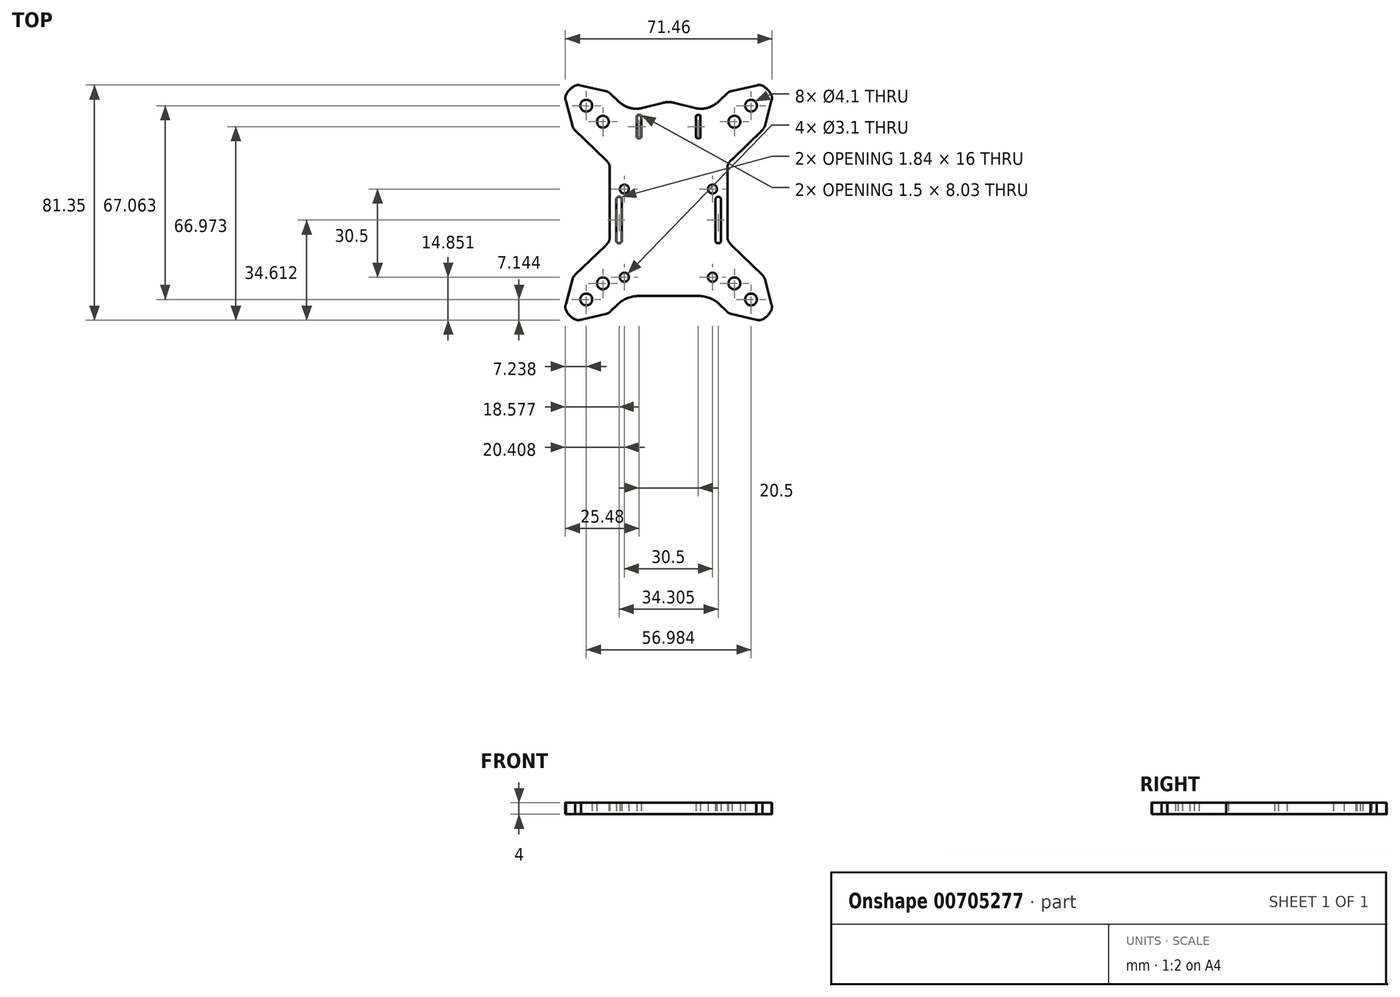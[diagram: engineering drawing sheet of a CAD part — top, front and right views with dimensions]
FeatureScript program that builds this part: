
annotation { "Feature Type Name" : "Feature", "Feature Type Description" : "" }
export const myFeature = defineFeature(function(context is Context, id is Id, definition is map)
    precondition{}
    {
        {
            var Q0;
            Q0=qCreatedBy(makeId("Top.planeOp"),FACE);
            var sketch = newSketch(context, id + "F0", { "sketchPlane" : qUnion([Q0])});
            skArc(sketch, "E0.MirrorCS", {"start": v(21.65, -41.5) * mm, "mid": v(20.88, -41.2) * mm, "end": v(20.23, -40.73) * mm});
            skArc(sketch, "E1.MirrorCS", {"start": v(32.4, -43.4) * mm, "mid": v(31.36, -43.62) * mm, "end": v(30.33, -43.46) * mm});
            skLineSegment(sketch, "E2.MirrorCS", {"start": v(19.47, -40) * mm, "end": v(20.23, -40.73) * mm});
            skArc(sketch, "E3.MirrorCS", {"start": v(35.55, -40.13) * mm, "mid": v(34.25, -42.03) * mm, "end": v(32.4, -43.4) * mm});
            skLineSegment(sketch, "E4.MirrorCS", {"start": v(30.33, -43.46) * mm, "end": v(25.04, -42.26) * mm});
            skLineSegment(sketch, "E5.MirrorCS", {"start": v(25.04, -42.26) * mm, "end": v(21.65, -41.5) * mm});
            skLineSegment(sketch, "E6.MirrorCS", {"start": v(34.15, -32.83) * mm, "end": v(33.26, -29.46) * mm});
            skArc(sketch, "E7.MirrorCS", {"start": v(32.45, -28.06) * mm, "mid": v(32.95, -28.7) * mm, "end": v(33.26, -29.46) * mm});
            skArc(sketch, "E8.MirrorCS", {"start": v(35.55, -40.13) * mm, "mid": v(35.73, -39.1) * mm, "end": v(35.54, -38.06) * mm});
            skLineSegment(sketch, "E9.MirrorCS", {"start": v(35.54, -38.06) * mm, "end": v(34.15, -32.83) * mm});
            skCircle(sketch, "E10.MirrorC", {"center": v(28.5, -36.48) * mm, "radius": 2.05 * mm});
            skLineSegment(sketch, "E11.MirrorCS", {"start": v(19.47, -40) * mm, "end": v(17.5, -38.1) * mm});
            skLineSegment(sketch, "E12.MirrorCS", {"start": v(-19.47, -40) * mm, "end": v(-20.23, -40.73) * mm});
            skArc(sketch, "E13.MirrorCS", {"start": v(-21.65, -41.5) * mm, "mid": v(-20.88, -41.2) * mm, "end": v(-20.23, -40.73) * mm});
            skArc(sketch, "E14.MirrorCS", {"start": v(-32.45, -28.06) * mm, "mid": v(-32.95, -28.7) * mm, "end": v(-33.26, -29.46) * mm});
            skArc(sketch, "E15.MirrorCS", {"start": v(-32.4, -43.4) * mm, "mid": v(-31.36, -43.62) * mm, "end": v(-30.33, -43.46) * mm});
            skLineSegment(sketch, "E16.MirrorCS", {"start": v(-25.04, -42.26) * mm, "end": v(-21.65, -41.5) * mm});
            skArc(sketch, "E17.MirrorCS", {"start": v(-35.55, -40.13) * mm, "mid": v(-35.73, -39.1) * mm, "end": v(-35.54, -38.06) * mm});
            skLineSegment(sketch, "E18.MirrorCS", {"start": v(-34.15, -32.83) * mm, "end": v(-33.26, -29.46) * mm});
            skArc(sketch, "E19.MirrorCS", {"start": v(-35.55, -40.13) * mm, "mid": v(-34.25, -42.03) * mm, "end": v(-32.4, -43.4) * mm});
            skCircle(sketch, "E20.MirrorC", {"center": v(-28.5, -36.48) * mm, "radius": 2.05 * mm});
            skLineSegment(sketch, "E21.MirrorCS", {"start": v(-35.54, -38.06) * mm, "end": v(-34.15, -32.83) * mm});
            skLineSegment(sketch, "E22.MirrorCS", {"start": v(-30.33, -43.46) * mm, "end": v(-25.04, -42.26) * mm});
            skLineSegment(sketch, "E23.MirrorCS", {"start": v(-19.47, -40) * mm, "end": v(-17.5, -38.1) * mm});
            skLineSegment(sketch, "E24.MirrorCS", {"start": v(-19.47, 34.1) * mm, "end": v(-20.23, 34.84) * mm});
            skArc(sketch, "E25.MirrorCS", {"start": v(-21.65, 35.6) * mm, "mid": v(-20.88, 35.32) * mm, "end": v(-20.23, 34.84) * mm});
            skArc(sketch, "E26.MirrorCS", {"start": v(-32.4, 37.52) * mm, "mid": v(-31.36, 37.73) * mm, "end": v(-30.33, 37.57) * mm});
            skLineSegment(sketch, "E27.MirrorCS", {"start": v(-25.04, 36.38) * mm, "end": v(-21.65, 35.6) * mm});
            skLineSegment(sketch, "E28.MirrorCS", {"start": v(-34.15, 26.94) * mm, "end": v(-33.26, 23.57) * mm});
            skArc(sketch, "E29.MirrorCS", {"start": v(-35.55, 34.24) * mm, "mid": v(-35.73, 33.2) * mm, "end": v(-35.54, 32.17) * mm});
            skArc(sketch, "E30.MirrorCS", {"start": v(-32.45, 22.18) * mm, "mid": v(-32.95, 22.82) * mm, "end": v(-33.26, 23.57) * mm});
            skArc(sketch, "E31.MirrorCS", {"start": v(-35.55, 34.24) * mm, "mid": v(-34.25, 36.14) * mm, "end": v(-32.4, 37.52) * mm});
            skCircle(sketch, "E32.MirrorC", {"center": v(-28.5, 30.59) * mm, "radius": 2.05 * mm});
            skCircle(sketch, "E33.MirrorC", {"center": v(-22.74, 25.03) * mm, "radius": 2.05 * mm});
            skLineSegment(sketch, "E34.MirrorCS", {"start": v(-30.33, 37.57) * mm, "end": v(-25.04, 36.38) * mm});
            skLineSegment(sketch, "E35.MirrorCS", {"start": v(-19.47, 34.1) * mm, "end": v(-17.5, 32.21) * mm});
            skLineSegment(sketch, "E36.MirrorCS", {"start": v(-35.54, 32.17) * mm, "end": v(-34.15, 26.94) * mm});
            skLineSegment(sketch, "E37", {"start": v(32.45, -28.06) * mm, "end": v(21.83, -17.82) * mm});
            skLineSegment(sketch, "E38.MirrorCS", {"start": v(-32.45, -28.06) * mm, "end": v(-21.83, -17.82) * mm});
            skLineSegment(sketch, "E39.MirrorCS", {"start": v(-32.45, 22.18) * mm, "end": v(-21.83, 11.93) * mm});
            skArc(sketch, "E40.filletArc", {"start": v(21.83, 11.93) * mm, "mid": v(21.43, 11.52) * mm, "end": v(21.05, 11.08) * mm});
            skArc(sketch, "E41.filletArc", {"start": v(-21.83, -17.82) * mm, "mid": v(-21.43, -17.4) * mm, "end": v(-21.05, -16.97) * mm});
            skArc(sketch, "E42.filletArc", {"start": v(-21.05, 11.08) * mm, "mid": v(-21.43, 11.52) * mm, "end": v(-21.83, 11.93) * mm});
            skLineSegment(sketch, "E43", {"start": v(10.56, -35.3) * mm, "end": v(-10.56, -35.3) * mm});
            skArc(sketch, "E44.filletArc", {"start": v(17.5, -38.1) * mm, "mid": v(14.3, -36.03) * mm, "end": v(10.56, -35.3) * mm});
            skArc(sketch, "E45.filletArc", {"start": v(-10.56, -35.3) * mm, "mid": v(-14.3, -36.03) * mm, "end": v(-17.5, -38.1) * mm});
            skPoint(sketch, "E46.middle", {"position": v(-0.07, 13.36) * mm});
            skArc(sketch, "E47.MirrorCS", {"start": v(-13.62, 29.89) * mm, "mid": v(-15.7, 30.83) * mm, "end": v(-17.5, 32.21) * mm});
            skArc(sketch, "E48.MirrorCS", {"start": v(17.5, 32.21) * mm, "mid": v(15.7, 30.83) * mm, "end": v(13.62, 29.89) * mm});
            skArc(sketch, "E49.MirrorCS", {"start": v(32.45, 22.18) * mm, "mid": v(32.95, 22.82) * mm, "end": v(33.26, 23.57) * mm});
            skLineSegment(sketch, "E50.MirrorCS", {"start": v(19.47, 34.1) * mm, "end": v(17.5, 32.21) * mm});
            skLineSegment(sketch, "E51.MirrorCS", {"start": v(19.47, 34.1) * mm, "end": v(20.23, 34.84) * mm});
            skLineSegment(sketch, "E52.MirrorCS", {"start": v(25.04, 36.38) * mm, "end": v(21.65, 35.6) * mm});
            skArc(sketch, "E53.MirrorCS", {"start": v(35.55, 34.24) * mm, "mid": v(35.73, 33.2) * mm, "end": v(35.54, 32.17) * mm});
            skArc(sketch, "E54.MirrorCS", {"start": v(32.4, 37.52) * mm, "mid": v(31.36, 37.73) * mm, "end": v(30.33, 37.57) * mm});
            skLineSegment(sketch, "E55.MirrorCS", {"start": v(34.15, 26.94) * mm, "end": v(33.26, 23.57) * mm});
            skArc(sketch, "E56.MirrorCS", {"start": v(21.65, 35.6) * mm, "mid": v(20.88, 35.32) * mm, "end": v(20.23, 34.84) * mm});
            skArc(sketch, "E57.MirrorCS", {"start": v(35.55, 34.24) * mm, "mid": v(34.25, 36.14) * mm, "end": v(32.4, 37.52) * mm});
            skLineSegment(sketch, "E58.MirrorCS", {"start": v(30.33, 37.57) * mm, "end": v(25.04, 36.38) * mm});
            skLineSegment(sketch, "E59.MirrorCS", {"start": v(35.54, 32.17) * mm, "end": v(34.15, 26.94) * mm});
            skCircle(sketch, "E60.MirrorC", {"center": v(28.5, 30.59) * mm, "radius": 2.05 * mm});
            skCircle(sketch, "E61.MirrorC", {"center": v(22.74, 25.03) * mm, "radius": 2.05 * mm});
            skLineSegment(sketch, "E62.MirrorCS", {"start": v(32.45, 22.18) * mm, "end": v(21.83, 11.93) * mm});
            skCircle(sketch, "E63.MirrorC", {"center": v(-22.74, -30.92) * mm, "radius": 2.05 * mm});
            skLineSegment(sketch, "E64", {"start": v(-9.22, 29.75) * mm, "end": v(-1.96, 31.58) * mm});
            skLineSegment(sketch, "E65", {"start": v(1.96, 31.58) * mm, "end": v(9.22, 29.75) * mm});
            skArc(sketch, "E66.filletArc", {"start": v(1.96, 31.58) * mm, "mid": v(0, 31.82) * mm, "end": v(-1.96, 31.58) * mm});
            skArc(sketch, "E67.filletArc", {"start": v(9.22, 29.75) * mm, "mid": v(11.43, 29.5) * mm, "end": v(13.62, 29.89) * mm});
            skArc(sketch, "E68.filletArc", {"start": v(-13.62, 29.89) * mm, "mid": v(-11.43, 29.5) * mm, "end": v(-9.22, 29.75) * mm});
            skLineSegment(sketch, "E69.bottom", {"start": v(17.93, -27.48) * mm, "end": v(-18.07, -27.48) * mm, "construction": true});
            skLineSegment(sketch, "E69.top", {"start": v(17.93, 7.48) * mm, "end": v(-18.07, 7.48) * mm, "construction": true});
            skCircle(sketch, "E70", {"center": v(15.18, -28.77) * mm, "radius": 1.55 * mm});
            skCircle(sketch, "E71", {"center": v(-15.32, -28.77) * mm, "radius": 1.55 * mm});
            skCircle(sketch, "E72", {"center": v(-15.32, 1.73) * mm, "radius": 1.55 * mm});
            skCircle(sketch, "E73", {"center": v(15.18, 1.73) * mm, "radius": 1.55 * mm});
            skLineSegment(sketch, "E74", {"start": v(21.83, -17.82) * mm, "end": v(21.05, -16.87) * mm});
            skCircle(sketch, "E75.MirrorC", {"center": v(22.74, -30.92) * mm, "radius": 2.05 * mm});
            skPoint(sketch, "E76.visualSharp", {"position": v(-20.44, 2.92) * mm});
            skArc(sketch, "E76.filletArc", {"start": v(-20.37, 9.18) * mm, "mid": v(-20.54, 10.19) * mm, "end": v(-21.05, 11.08) * mm});
            skPoint(sketch, "E77.visualSharp", {"position": v(-20.44, -12.47) * mm});
            skArc(sketch, "E77.filletArc", {"start": v(-21.05, -16.97) * mm, "mid": v(-20.54, -16.08) * mm, "end": v(-20.37, -15.07) * mm});
            skArc(sketch, "E78.filletArc", {"start": v(20.37, -14.96) * mm, "mid": v(20.54, -15.97) * mm, "end": v(21.05, -16.87) * mm});
            skPoint(sketch, "E79.visualSharp", {"position": v(20.3, 6.56) * mm});
            skArc(sketch, "E79.filletArc", {"start": v(21.05, 11.08) * mm, "mid": v(20.54, 10.19) * mm, "end": v(20.37, 9.18) * mm});
            skLineSegment(sketch, "E80", {"start": v(-28.5, -36.48) * mm, "end": v(-22.74, -30.92) * mm, "construction": true});
            skLineSegment(sketch, "E81", {"start": v(-22.74, -30.92) * mm, "end": v(-13.4, -21.92) * mm, "construction": true});
            skPoint(sketch, "E82", {"position": v(-18.07, -31.48) * mm});
            skLineSegment(sketch, "E83.bottom", {"start": v(9.5, 14.5) * mm, "end": v(-9.5, 14.5) * mm, "construction": true});
            skLineSegment(sketch, "E83.top", {"start": v(9.5, 33.5) * mm, "end": v(-9.5, 33.5) * mm, "construction": true});
            skPoint(sketch, "E83.middle", {"position": v(0, 24) * mm});
            skPoint(sketch, "E84", {"position": v(-9.5, 24) * mm});
            skPoint(sketch, "E85", {"position": v(9.5, 24) * mm});
            skPoint(sketch, "E86.middle.positionSnap0", {"position": v(-17.37, -10.07) * mm});
            skPoint(sketch, "E86.centerSnap0", {"position": v(-17.37, -10.07) * mm});
            skLineSegment(sketch, "E87", {"start": v(-15.32, 1.73) * mm, "end": v(-10.07, 1.73) * mm, "construction": true});
            skLineSegment(sketch, "E88.bottom", {"start": v(-16.93, -17) * mm, "end": v(-17.37, -17) * mm});
            skLineSegment(sketch, "E88.top", {"start": v(-16.93, -1) * mm, "end": v(-17.37, -1) * mm});
            skLineSegment(sketch, "E88.left", {"start": v(-16.23, -16.3) * mm, "end": v(-16.23, -1.7) * mm});
            skLineSegment(sketch, "E88.right", {"start": v(-18.07, -16.3) * mm, "end": v(-18.07, -1.7) * mm});
            skPoint(sketch, "E89.visualSharp", {"position": v(-16.23, -1) * mm});
            skArc(sketch, "E89.filletArc", {"start": v(-16.23, -1.7) * mm, "mid": v(-16.44, -1.21) * mm, "end": v(-16.93, -1) * mm});
            skPoint(sketch, "E90.visualSharp", {"position": v(-18.07, -1) * mm});
            skArc(sketch, "E90.filletArc", {"start": v(-17.37, -1) * mm, "mid": v(-17.87, -1.21) * mm, "end": v(-18.07, -1.7) * mm});
            skPoint(sketch, "E91.visualSharp", {"position": v(-16.23, -17) * mm});
            skArc(sketch, "E91.filletArc", {"start": v(-16.93, -17) * mm, "mid": v(-16.44, -16.8) * mm, "end": v(-16.23, -16.3) * mm});
            skPoint(sketch, "E92.visualSharp", {"position": v(-18.07, -17) * mm});
            skArc(sketch, "E92.filletArc", {"start": v(-18.07, -16.3) * mm, "mid": v(-17.87, -16.8) * mm, "end": v(-17.37, -17) * mm});
            skPoint(sketch, "E93.MirrorP", {"position": v(18.77, 6.75) * mm});
            skPoint(sketch, "E94.oppositeSnap0", {"position": v(-11.43, 29.5) * mm});
            skPoint(sketch, "E95.orphan", {"position": v(-9.5, 7.47) * mm});
            skLineSegment(sketch, "E96.bottom", {"start": v(-9.9, 27.37) * mm, "end": v(-10.6, 27.37) * mm});
            skLineSegment(sketch, "E96.top", {"start": v(-9.9, 19.34) * mm, "end": v(-10.6, 19.34) * mm});
            skLineSegment(sketch, "E96.left", {"start": v(-9.5, 26.97) * mm, "end": v(-9.5, 19.74) * mm});
            skLineSegment(sketch, "E96.right", {"start": v(-11, 26.97) * mm, "end": v(-11, 19.74) * mm});
            skLineSegment(sketch, "E97.MirrorCS", {"start": v(9.5, 26.97) * mm, "end": v(9.5, 24) * mm});
            skLineSegment(sketch, "E98.MirrorCS", {"start": v(9.9, 27.37) * mm, "end": v(10.6, 27.37) * mm});
            skLineSegment(sketch, "E99.MirrorCS", {"start": v(11, 26.97) * mm, "end": v(11, 19.74) * mm});
            skLineSegment(sketch, "E100.MirrorCS", {"start": v(9.5, 24) * mm, "end": v(9.5, 19.74) * mm});
            skLineSegment(sketch, "E101.MirrorCS", {"start": v(9.9, 19.34) * mm, "end": v(10.6, 19.34) * mm});
            skPoint(sketch, "E102.visualSharp", {"position": v(-11, 27.37) * mm});
            skArc(sketch, "E102.filletArc", {"start": v(-10.6, 27.37) * mm, "mid": v(-10.88, 27.25) * mm, "end": v(-11, 26.97) * mm});
            skPoint(sketch, "E103.visualSharp", {"position": v(-9.5, 19.34) * mm});
            skArc(sketch, "E103.filletArc", {"start": v(-9.9, 19.34) * mm, "mid": v(-9.62, 19.46) * mm, "end": v(-9.5, 19.74) * mm});
            skPoint(sketch, "E104.visualSharp", {"position": v(-11, 19.34) * mm});
            skArc(sketch, "E104.filletArc", {"start": v(-11, 19.74) * mm, "mid": v(-10.88, 19.46) * mm, "end": v(-10.6, 19.34) * mm});
            skPoint(sketch, "E105.visualSharp", {"position": v(11, 19.34) * mm});
            skArc(sketch, "E105.filletArc", {"start": v(10.6, 19.34) * mm, "mid": v(10.88, 19.46) * mm, "end": v(11, 19.74) * mm});
            skPoint(sketch, "E106.visualSharp", {"position": v(11, 27.37) * mm});
            skArc(sketch, "E106.filletArc", {"start": v(11, 26.97) * mm, "mid": v(10.88, 27.25) * mm, "end": v(10.6, 27.37) * mm});
            skPoint(sketch, "E107.visualSharp", {"position": v(9.5, 19.34) * mm});
            skArc(sketch, "E107.filletArc", {"start": v(9.5, 19.74) * mm, "mid": v(9.62, 19.46) * mm, "end": v(9.9, 19.34) * mm});
            skPoint(sketch, "E108.visualSharp", {"position": v(-9.5, 27.37) * mm});
            skArc(sketch, "E108.filletArc", {"start": v(-9.5, 26.97) * mm, "mid": v(-9.62, 27.25) * mm, "end": v(-9.9, 27.37) * mm});
            skLineSegment(sketch, "E109.trimOffspring", {"start": v(9.5, 29.68) * mm, "end": v(9.5, 33.5) * mm, "construction": true});
            skPoint(sketch, "E110.MirrorCS.start.orphan", {"position": v(9.5, 27.37) * mm});
            skPoint(sketch, "E111.orphan", {"position": v(9.5, 7.47) * mm});
            skArc(sketch, "E112.filletArc", {"start": v(9.9, 27.37) * mm, "mid": v(9.62, 27.25) * mm, "end": v(9.5, 26.97) * mm});
            skLineSegment(sketch, "E113", {"start": v(-20.37, 9.18) * mm, "end": v(-20.37, -15.07) * mm});
            skLineSegment(sketch, "E114", {"start": v(20.37, 9.18) * mm, "end": v(20.37, -14.96) * mm});
            skLineSegment(sketch, "E115.MirrorCS", {"start": v(16.93, -17) * mm, "end": v(17.37, -17) * mm});
            skLineSegment(sketch, "E116.MirrorCS", {"start": v(16.93, -1) * mm, "end": v(17.37, -1) * mm});
            skPoint(sketch, "E117.MirrorP", {"position": v(17.37, -10.07) * mm});
            skArc(sketch, "E118.MirrorCS", {"start": v(16.23, -1.7) * mm, "mid": v(16.44, -1.21) * mm, "end": v(16.93, -1) * mm});
            skArc(sketch, "E119.MirrorCS", {"start": v(17.37, -1) * mm, "mid": v(17.87, -1.21) * mm, "end": v(18.07, -1.7) * mm});
            skArc(sketch, "E120.MirrorCS", {"start": v(18.07, -16.3) * mm, "mid": v(17.87, -16.8) * mm, "end": v(17.37, -17) * mm});
            skPoint(sketch, "E121.MirrorP", {"position": v(16.23, -17) * mm});
            skArc(sketch, "E122.MirrorCS", {"start": v(16.93, -17) * mm, "mid": v(16.44, -16.8) * mm, "end": v(16.23, -16.3) * mm});
            skPoint(sketch, "E123.MirrorP", {"position": v(16.23, -1) * mm});
            skLineSegment(sketch, "E124.MirrorCS", {"start": v(16.23, -16.3) * mm, "end": v(16.23, -1.7) * mm});
            skPoint(sketch, "E125.MirrorP", {"position": v(18.07, -1) * mm});
            skPoint(sketch, "E126.MirrorP", {"position": v(18.07, -17) * mm});
            skLineSegment(sketch, "E127.MirrorCS", {"start": v(18.07, -16.3) * mm, "end": v(18.07, -1.7) * mm});
            skSolve(sketch);
        }
        {
            var Q0;
            Q0 = qSketchRegion(id + "F0", true);
            extrude(context, id + "F1", {"entities" : qUnion([Q0]), "depth" : 4 * mm, "offsetDistance" : 25 * mm});
        }
    });
